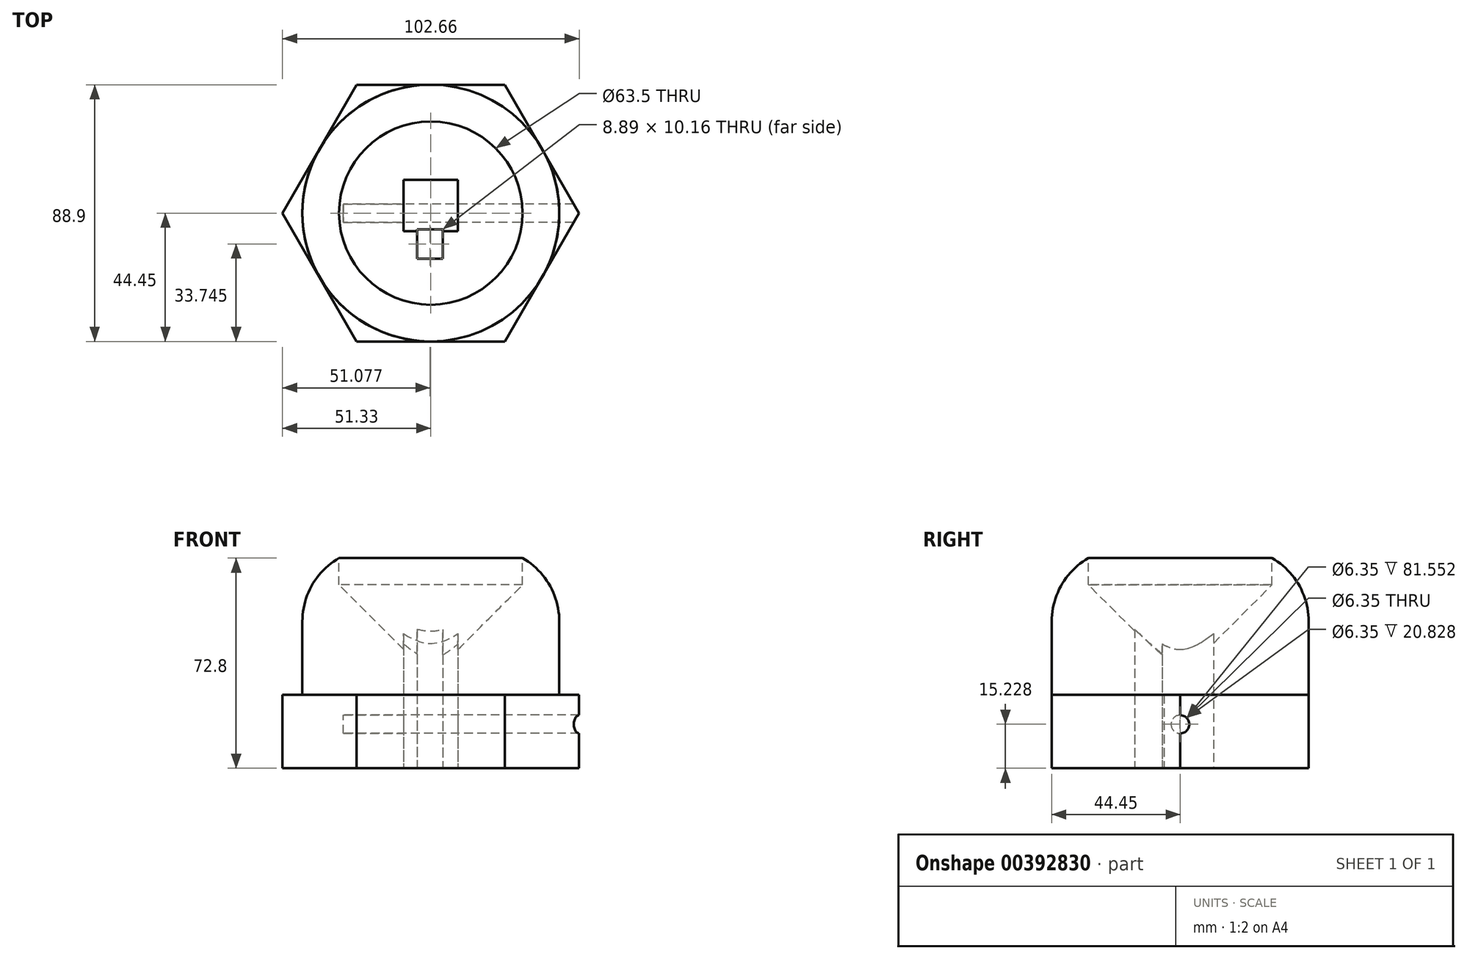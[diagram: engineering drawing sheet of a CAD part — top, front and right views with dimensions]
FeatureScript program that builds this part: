
annotation { "Feature Type Name" : "Feature", "Feature Type Description" : "" }
export const myFeature = defineFeature(function(context is Context, id is Id, definition is map)
    precondition{}
    {
        {
            var Q0;
            Q0=qCreatedBy(makeId("Top.planeOp"),FACE);
            var sketch = newSketch(context, id + "F0", { "sketchPlane" : qUnion([Q0])});
            skCircle(sketch, "E0", {"center": v(0, 0) * mm, "radius": 44.45 * mm});
            skSolve(sketch);
        }
        {
            var Q0;
            Q0=makeQuery(id+"F0.imprint","IMPRINT",FACE,{"disambiguationData":[TD([[makeQuery(id+"F0.imprint","IMPRINT",EDGE,{"derivedFrom":sQuery(id+"F0.wireOp",EDGE,"E0")}),1.0]])]});
            extrude(context, id + "F1", {"entities" : qUnion([Q0]), "oppositeDirection" : true, "depth" : 50.8 * mm});
        }
        {
            var Q0;
            Q0=makeQuery(id+"F1.opExtrude","CAP_EDGE",EDGE,{"disambiguationData":[OSD([sQuery(id+"F0.wireOp",EDGE,"E0")])],"isStart":true});
            fillet(context, id + "F2", {"entities" : qUnion([Q0]), "radius" : 25.4 * mm, "tangentPropagation" : true, "allowEdgeOverflow" : false});
        }
        {
            var Q0;
            Q0=makeQuery(id+"F1.opExtrude","CAP_FACE",FACE,{"disambiguationData":[OSD([sQuery(id+"F0.wireOp",EDGE,"E0")])],"isStart":true});
            var sketch = newSketch(context, id + "F3", { "sketchPlane" : qUnion([Q0])});
            skCircle(sketch, "E1", {"center": v(0, 0) * mm, "radius": 31.75 * mm});
            skSolve(sketch);
        }
        {
            var Q0;
            Q0=makeQuery(id+"F3.imprint","IMPRINT",FACE,{"disambiguationData":[TD([[makeQuery(id+"F3.imprint","IMPRINT",EDGE,{"derivedFrom":sQuery(id+"F3.wireOp",EDGE,"E1")}),1.0]])]});
            var Q1;
            {var subQ0=sQuery(id+"F0.wireOp",EDGE,"E0");Q1=makeQuery(id+"F3.imprint","IMPRINT",FACE,{"disambiguationData":[TD([[makeQuery(id+"F3.imprint","IMPRINT",EDGE,{"derivedFrom":makeQuery(id+"F2.opFillet","BLEND_EDGE",EDGE,{"blendedFrom":[makeQuery(id+"F1.opExtrude","CAP_EDGE",EDGE,{"disambiguationData":[OSD([subQ0])],"isStart":true}),makeQuery(id+"F1.opExtrude","CAP_FACE",FACE,{"disambiguationData":[OSD([subQ0])],"isStart":true})],"blendedInto":[makeQuery(id+"F1.opExtrude","CAP_FACE",FACE,{"disambiguationData":[OSD([subQ0])],"isStart":true})]})}),1.0]])]});}
            extrude(context, id + "F4", {"entities" : qUnion([Q0, Q1]), "operationType" : NewBodyOperationType.REMOVE, "oppositeDirection" : true, "depth" : 38.1 * mm});
        }
        {
            var Q0;
            Q0=makeQuery(id+"F4.boolean.opBoolean","COPY",EDGE,{"derivedFrom":makeQuery(id+"F4.opExtrude","CAP_EDGE",EDGE,{"disambiguationData":[OSD([sQuery(id+"F3.wireOp",EDGE,"E1")])],"isStart":false})});
            chamfer(context, id + "F5", {"entities" : qUnion([Q0]), "width" : 25.4 * mm, "tangentPropagation" : true});
        }
        {
            var Q0;
            Q0=makeQuery(id+"F4.boolean.opBoolean","COPY",FACE,{"derivedFrom":makeQuery(id+"F4.opExtrude","CAP_FACE",FACE,{"disambiguationData":[OSD([sQuery(id+"F3.wireOp",EDGE,"E1")])],"isStart":false})});
            extrude(context, id + "F6", {"entities" : qUnion([Q0]), "operationType" : NewBodyOperationType.REMOVE, "oppositeDirection" : true, "depth" : 25.4 * mm});
        }
        {
            var Q0;
            Q0=makeQuery(id+"F1.opExtrude","CAP_FACE",FACE,{"disambiguationData":[OSD([sQuery(id+"F0.wireOp",EDGE,"E0")])],"isStart":false});
            var sketch = newSketch(context, id + "F7", { "sketchPlane" : qUnion([Q0])});
            skCircle(sketch, "E2.cCircle", {"center": v(0, 0) * mm, "radius": 44.45 * mm, "construction": true});
            skLineSegment(sketch, "E2.0", {"start": v(-25.66, 44.45) * mm, "end": v(25.66, 44.45) * mm});
            skLineSegment(sketch, "E2.1", {"start": v(25.66, 44.45) * mm, "end": v(51.33, 0) * mm});
            skLineSegment(sketch, "E2.2", {"start": v(51.33, 0) * mm, "end": v(25.66, -44.45) * mm});
            skLineSegment(sketch, "E2.3", {"start": v(25.66, -44.45) * mm, "end": v(-25.66, -44.45) * mm});
            skLineSegment(sketch, "E2.4", {"start": v(-25.66, -44.45) * mm, "end": v(-51.33, 0) * mm});
            skLineSegment(sketch, "E2.5", {"start": v(-51.33, 0) * mm, "end": v(-25.66, 44.45) * mm});
            skPoint(sketch, "E2.0.midPoint", {"position": v(0, 44.45) * mm});
            skSolve(sketch);
        }
        {
            var Q0;
            {var subQ0=sQuery(id+"F7.wireOp",EDGE,"E2.1");var subQ1=sQuery(id+"F7.wireOp",EDGE,"E2.0");var subQ2=makeQuery(id+"F7.imprint","INTERSECT",VERTEX,{"derivedFrom":[subQ1,subQ0]});Q0=makeQuery(id+"F7.imprint","IMPRINT",FACE,{"disambiguationData":[TD([[makeQuery(id+"F7.imprint","IMPRINT",EDGE,{"disambiguationData":[TD([[subQ2,1.0]])],"derivedFrom":subQ1}),-1.0]])]});}
            var Q1;
            {var subQ0=sQuery(id+"F7.wireOp",EDGE,"E2.5");var subQ1=sQuery(id+"F7.wireOp",EDGE,"E2.0");var subQ2=makeQuery(id+"F7.imprint","INTERSECT",VERTEX,{"derivedFrom":[subQ1,subQ0]});Q1=makeQuery(id+"F7.imprint","IMPRINT",FACE,{"disambiguationData":[TD([[makeQuery(id+"F7.imprint","IMPRINT",EDGE,{"disambiguationData":[TD([[subQ2,-1.0]])],"derivedFrom":subQ1}),-1.0]])]});}
            var Q2;
            {var subQ0=sQuery(id+"F7.wireOp",EDGE,"E2.5");var subQ1=sQuery(id+"F7.wireOp",EDGE,"E2.4");var subQ2=makeQuery(id+"F7.imprint","INTERSECT",VERTEX,{"derivedFrom":[subQ1,subQ0]});Q2=makeQuery(id+"F7.imprint","IMPRINT",FACE,{"disambiguationData":[TD([[makeQuery(id+"F7.imprint","IMPRINT",EDGE,{"disambiguationData":[TD([[subQ2,1.0]])],"derivedFrom":subQ1}),-1.0]])]});}
            var Q3;
            {var subQ0=sQuery(id+"F0.wireOp",EDGE,"E0");Q3=makeQuery(id+"F7.imprint","IMPRINT",FACE,{"disambiguationData":[TD([[makeQuery(id+"F7.imprint","IMPRINT",EDGE,{"derivedFrom":makeQuery(id+"F6.boolean.opBoolean","INTERSECT",EDGE,{"derivedFrom":[makeQuery(id+"F1.opExtrude","CAP_FACE",FACE,{"disambiguationData":[OSD([subQ0])],"isStart":false}),makeQuery(id+"F6.opExtrude","SWEPT_FACE",FACE,{"disambiguationData":[OSD([sQuery(id+"F3.wireOp",EDGE,"E1")])]})]})}),1.0]])]});}
            var Q4;
            {var subQ0=sQuery(id+"F7.wireOp",EDGE,"E2.4");var subQ1=sQuery(id+"F7.wireOp",EDGE,"E2.3");var subQ2=makeQuery(id+"F7.imprint","INTERSECT",VERTEX,{"derivedFrom":[subQ1,subQ0]});Q4=makeQuery(id+"F7.imprint","IMPRINT",FACE,{"disambiguationData":[TD([[makeQuery(id+"F7.imprint","IMPRINT",EDGE,{"disambiguationData":[TD([[subQ2,1.0]])],"derivedFrom":subQ1}),-1.0]])]});}
            var Q5;
            {var subQ0=sQuery(id+"F7.wireOp",EDGE,"E2.3");var subQ1=sQuery(id+"F7.wireOp",EDGE,"E2.2");var subQ2=makeQuery(id+"F7.imprint","INTERSECT",VERTEX,{"derivedFrom":[subQ1,subQ0]});Q5=makeQuery(id+"F7.imprint","IMPRINT",FACE,{"disambiguationData":[TD([[makeQuery(id+"F7.imprint","IMPRINT",EDGE,{"disambiguationData":[TD([[subQ2,1.0]])],"derivedFrom":subQ1}),-1.0]])]});}
            var Q6;
            {var subQ0=sQuery(id+"F7.wireOp",EDGE,"E2.2");var subQ1=sQuery(id+"F7.wireOp",EDGE,"E2.1");var subQ2=makeQuery(id+"F7.imprint","INTERSECT",VERTEX,{"derivedFrom":[subQ1,subQ0]});Q6=makeQuery(id+"F7.imprint","IMPRINT",FACE,{"disambiguationData":[TD([[makeQuery(id+"F7.imprint","IMPRINT",EDGE,{"disambiguationData":[TD([[subQ2,1.0]])],"derivedFrom":subQ1}),-1.0]])]});}
            extrude(context, id + "F8", {"entities" : qUnion([Q0, Q1, Q2, Q3, Q4, Q5, Q6]), "operationType" : NewBodyOperationType.ADD, "depth" : 25.4 * mm});
        }
        {
            var Q0;
            Q0=makeQuery(id+"F8.opExtrude","CAP_FACE",FACE,{"disambiguationData":[OSD([sQuery(id+"F0.wireOp",EDGE,"E0"),sQuery(id+"F3.wireOp",EDGE,"E1"),sQuery(id+"F7.wireOp",EDGE,"E2.0"),sQuery(id+"F7.wireOp",EDGE,"E2.1"),sQuery(id+"F7.wireOp",EDGE,"E2.2"),sQuery(id+"F7.wireOp",EDGE,"E2.3"),sQuery(id+"F7.wireOp",EDGE,"E2.4"),sQuery(id+"F7.wireOp",EDGE,"E2.5")])],"isStart":false});
            var sketch = newSketch(context, id + "F9", { "sketchPlane" : qUnion([Q0])});
            skLineSegment(sketch, "E3.bottom", {"start": v(-9.4, 6.28) * mm, "end": v(0, 6.28) * mm});
            skLineSegment(sketch, "E3.top", {"start": v(-9.4, -11.5) * mm, "end": v(0, -11.5) * mm});
            skLineSegment(sketch, "E3.left", {"start": v(-9.4, 6.28) * mm, "end": v(-9.4, -11.5) * mm});
            skLineSegment(sketch, "E3.right", {"start": v(0, 6.28) * mm, "end": v(0, -11.5) * mm});
            skLineSegment(sketch, "E4.bottom", {"start": v(0, 6.28) * mm, "end": v(9.4, 6.28) * mm});
            skLineSegment(sketch, "E4.top", {"start": v(0, -11.5) * mm, "end": v(9.4, -11.5) * mm});
            skLineSegment(sketch, "E4.right", {"start": v(9.4, 6.28) * mm, "end": v(9.4, -11.5) * mm});
            skSolve(sketch);
        }
        {
            var Q0;
            Q0=makeQuery(id+"F9.imprint","IMPRINT",FACE,{"disambiguationData":[TD([[makeQuery(id+"F9.imprint","IMPRINT",EDGE,{"derivedFrom":sQuery(id+"F9.wireOp",EDGE,"E3.top")}),-1.0]])]});
            var sketch = newSketch(context, id + "F10", { "sketchPlane" : qUnion([Q0])});
            skLineSegment(sketch, "E5.bottom", {"start": v(-4.7, 5.62) * mm, "end": v(4.2, 5.62) * mm});
            skLineSegment(sketch, "E5.top", {"start": v(-4.7, 15.78) * mm, "end": v(4.2, 15.78) * mm});
            skLineSegment(sketch, "E5.left", {"start": v(-4.7, 5.62) * mm, "end": v(-4.7, 15.78) * mm});
            skLineSegment(sketch, "E5.right", {"start": v(4.2, 5.62) * mm, "end": v(4.2, 15.78) * mm});
            skSolve(sketch);
        }
        {
            var Q0;
            {var subQ2=sQuery(id+"F9.wireOp",EDGE,"E4.top");Q0=makeQuery(id+"F9.imprint","IMPRINT",FACE,{"disambiguationData":[TD([[makeQuery(id+"F9.imprint","IMPRINT",EDGE,{"derivedFrom":subQ2}),1.0]])]});}
            var Q1;
            {var subQ1=sQuery(id+"F9.wireOp",EDGE,"E3.top");Q1=makeQuery(id+"F9.imprint","IMPRINT",FACE,{"disambiguationData":[TD([[makeQuery(id+"F9.imprint","IMPRINT",EDGE,{"derivedFrom":subQ1}),1.0]])]});}
            extrude(context, id + "F11", {"entities" : qUnion([Q0, Q1]), "operationType" : NewBodyOperationType.REMOVE, "oppositeDirection" : true, "depth" : 25.4 * mm});
        }
        {
            var Q0;
            {var subQ1=sQuery(id+"F10.wireOp",EDGE,"E5.top");Q0=makeQuery(id+"F10.imprint","IMPRINT",FACE,{"disambiguationData":[TD([[makeQuery(id+"F10.imprint","IMPRINT",EDGE,{"derivedFrom":subQ1}),-1.0]])]});}
            var Q1;
            {var subQ8=sQuery(id+"F10.wireOp",EDGE,"E5.bottom");Q1=makeQuery(id+"F10.imprint","IMPRINT",FACE,{"disambiguationData":[TD([[makeQuery(id+"F10.imprint","IMPRINT",EDGE,{"derivedFrom":subQ8}),-1.0]])]});}
            extrude(context, id + "F12", {"entities" : qUnion([Q0, Q1]), "operationType" : NewBodyOperationType.REMOVE, "oppositeDirection" : true, "depth" : 66.3 * mm});
        }
        {
            var Q0;
            {var subQ0=sQuery(id+"F10.wireOp",EDGE,"E5.left");var subQ1=sQuery(id+"F10.wireOp",EDGE,"E5.bottom");var subQ2=sQuery(id+"F9.wireOp",EDGE,"E3.left");var subQ3=sQuery(id+"F9.wireOp",EDGE,"E3.bottom");var subQ4=sQuery(id+"F3.wireOp",EDGE,"E1");var subQ5=sQuery(id+"F0.wireOp",EDGE,"E0");var subQ10=sQuery(id+"F9.wireOp",EDGE,"E4.bottom");Q0=makeQuery(id+"F12.boolean.opBoolean","SPLIT",FACE,{"disambiguationData":[TD([makeQuery(id+"F12.opExtrude","SWEPT_FACE",FACE,{"disambiguationData":[OSD([subQ0]),TDD([makeQuery(id+"F10.imprint","IMPRINT",EDGE,{"disambiguationData":[TD([[makeQuery(id+"F10.imprint","INTERSECT",VERTEX,{"derivedFrom":[subQ1,subQ0]}),-1.0]])],"derivedFrom":subQ0})])]})])],"derivedFrom":makeQuery(id+"F11.boolean.opBoolean","COPY",FACE,{"derivedFrom":makeQuery(id+"F11.opExtrude","CAP_FACE",FACE,{"disambiguationData":[OSD([subQ5,subQ4,subQ3,sQuery(id+"F9.wireOp",EDGE,"E3.top"),subQ2,subQ10,sQuery(id+"F9.wireOp",EDGE,"E4.top"),sQuery(id+"F9.wireOp",EDGE,"E4.right")])],"isStart":false})})});}
            var Q1;
            {var subQ0=sQuery(id+"F10.wireOp",EDGE,"E5.right");var subQ1=sQuery(id+"F10.wireOp",EDGE,"E5.bottom");var subQ2=sQuery(id+"F9.wireOp",EDGE,"E4.right");var subQ3=sQuery(id+"F9.wireOp",EDGE,"E4.bottom");var subQ4=sQuery(id+"F3.wireOp",EDGE,"E1");var subQ5=sQuery(id+"F0.wireOp",EDGE,"E0");var subQ10=sQuery(id+"F9.wireOp",EDGE,"E3.bottom");Q1=makeQuery(id+"F12.boolean.opBoolean","SPLIT",FACE,{"disambiguationData":[TD([makeQuery(id+"F12.opExtrude","SWEPT_FACE",FACE,{"disambiguationData":[OSD([subQ0]),TDD([makeQuery(id+"F10.imprint","IMPRINT",EDGE,{"disambiguationData":[TD([[makeQuery(id+"F10.imprint","INTERSECT",VERTEX,{"derivedFrom":[subQ1,subQ0]}),-1.0]])],"derivedFrom":subQ0})])]})])],"derivedFrom":makeQuery(id+"F11.boolean.opBoolean","COPY",FACE,{"derivedFrom":makeQuery(id+"F11.opExtrude","CAP_FACE",FACE,{"disambiguationData":[OSD([subQ5,subQ4,subQ10,sQuery(id+"F9.wireOp",EDGE,"E3.top"),sQuery(id+"F9.wireOp",EDGE,"E3.left"),subQ3,sQuery(id+"F9.wireOp",EDGE,"E4.top"),subQ2])],"isStart":false})})});}
            extrude(context, id + "F13", {"entities" : qUnion([Q0, Q1]), "operationType" : NewBodyOperationType.REMOVE, "oppositeDirection" : true, "depth" : 50.8 * mm});
        }
        {
            var Q0;
            Q0=qSketchRegion(id+"F7",true);
            var Q1;
            Q1=qSketchRegion(id+"F10",true);
            extrude(context, id + "F14", {"entities" : qUnion([Q0, Q1]), "depth" : 25.4 * mm});
        }
        {
            var Q0;
            Q0=makeQuery(id+"F14.opExtrude","CAP_FACE",FACE,{"disambiguationData":[OSD([sQuery(id+"F10.wireOp",EDGE,"E5.bottom"),sQuery(id+"F10.wireOp",EDGE,"E5.top"),sQuery(id+"F10.wireOp",EDGE,"E5.left"),sQuery(id+"F10.wireOp",EDGE,"E5.right")])],"isStart":false});
            extrude(context, id + "F15", {"entities" : qUnion([Q0]), "operationType" : NewBodyOperationType.REMOVE, "oppositeDirection" : true, "depth" : 50.8 * mm});
        }
        {
            var Q0;
            Q0=qCreatedBy(makeId("Right.planeOp"),FACE);
            var sketch = newSketch(context, id + "F16", { "sketchPlane" : qUnion([Q0])});
            skCircle(sketch, "E6", {"center": v(0, -60.97) * mm, "radius": 3.18 * mm});
            skSolve(sketch);
        }
        {
            var Q0;
            Q0=makeQuery(id+"F16.imprint","IMPRINT",FACE,{"disambiguationData":[TD([[makeQuery(id+"F16.imprint","IMPRINT",EDGE,{"derivedFrom":sQuery(id+"F16.wireOp",EDGE,"E6")}),1.0]])]});
            extrude(context, id + "F17", {"entities" : qUnion([Q0]), "operationType" : NewBodyOperationType.REMOVE, "depth" : 143 * mm, "hasSecondDirection" : true, "secondDirectionOppositeDirection" : true, "secondDirectionDepth" : 4.83 * mm});
        }
        {
            var Q0;
            Q0=makeQuery(id+"F17.boolean.opBoolean","COPY",FACE,{"derivedFrom":makeQuery(id+"F17.opExtrude","CAP_FACE",FACE,{"disambiguationData":[OSD([sQuery(id+"F16.wireOp",EDGE,"E6")])],"isStart":true})});
            extrude(context, id + "F18", {"entities" : qUnion([Q0]), "operationType" : NewBodyOperationType.REMOVE, "oppositeDirection" : true, "depth" : 25.4 * mm});
        }
    });
